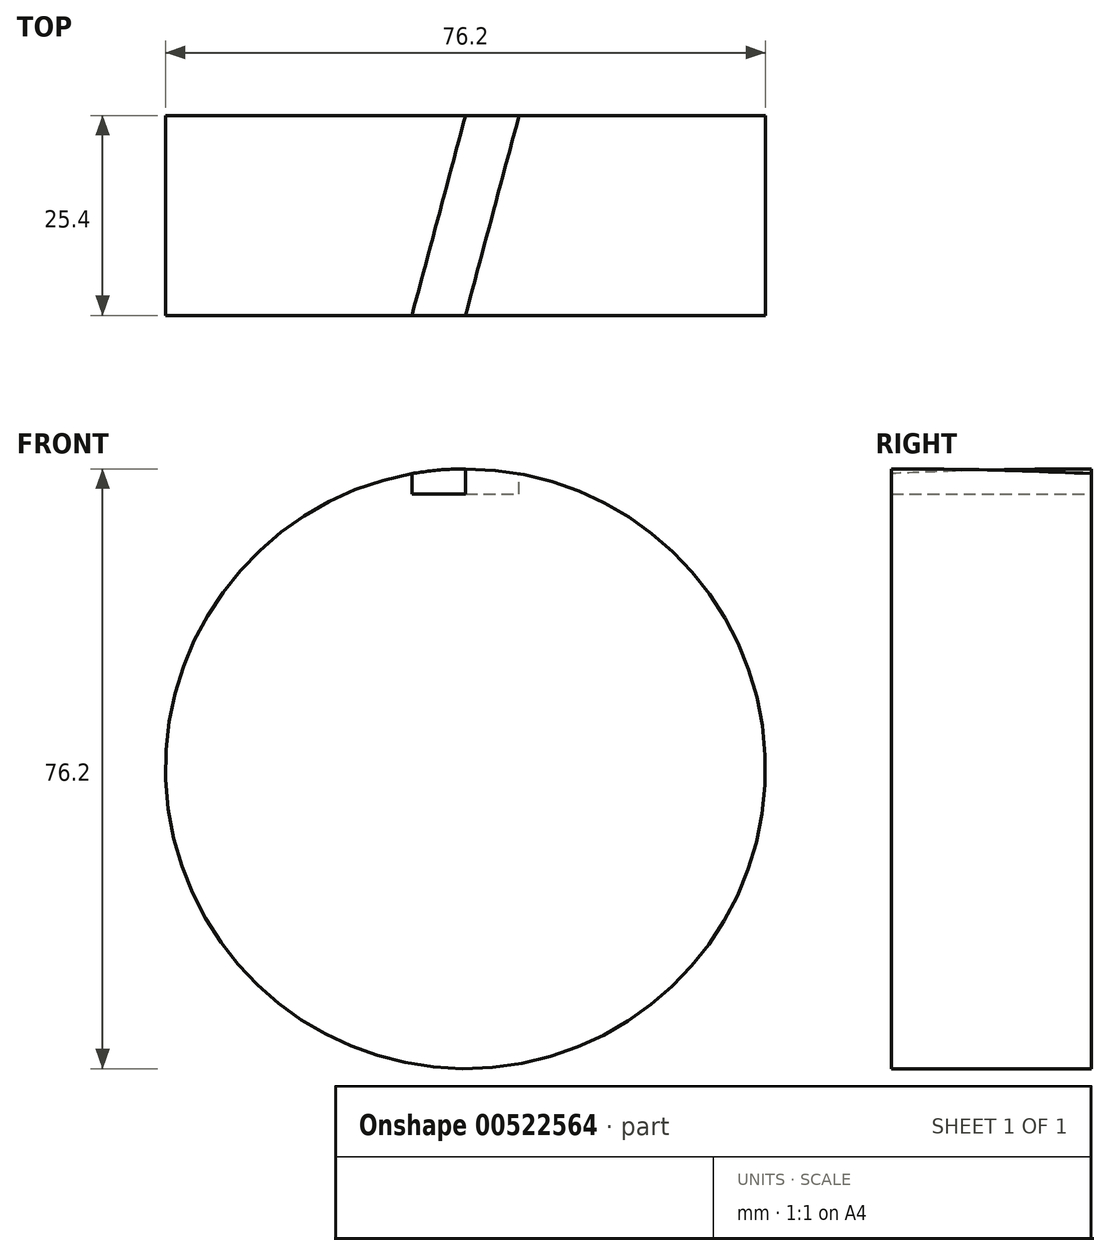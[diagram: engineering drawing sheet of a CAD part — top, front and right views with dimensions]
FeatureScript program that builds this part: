
annotation { "Feature Type Name" : "Feature", "Feature Type Description" : "" }
export const myFeature = defineFeature(function(context is Context, id is Id, definition is map)
    precondition{}
    {
        {
            var Q0;
            Q0=qCreatedBy(makeId("Front.planeOp"),FACE);
            var sketch = newSketch(context, id + "F0", { "sketchPlane" : qUnion([Q0])});
            skCircle(sketch, "E0", {"center": v(0, 0) * mm, "radius": 38.1 * mm});
            skSolve(sketch);
        }
        {
            var Q0;
            Q0 = qSketchRegion(id + "F0", true);
            extrude(context, id + "F1", {"entities" : qUnion([Q0]), "endBound" : BoundingType.SYMMETRIC, "depth" : 25.4 * mm, "offsetDistance" : 25.4 * mm});
        }
        {
            var Q0;
            Q0=qCreatedBy(makeId("Top.planeOp"),FACE);
            cPlane(context, id + "F2", {"entities" : qUnion([Q0]), "cplaneType" : CPlaneType.OFFSET, "offset" : 38.1 * mm, "width" : 152.4 * mm, "height" : 152.4 * mm});
        }
        {
            var Q0;
            Q0=qCreatedBy(id+"F2.planeOp",FACE);
            var sketch = newSketch(context, id + "F3", { "sketchPlane" : qUnion([Q0])});
            skLineSegment(sketch, "E1", {"start": v(0, -12.7) * mm, "end": v(-6.8, -12.7) * mm});
            skLineSegment(sketch, "E2", {"start": v(-6.8, -12.7) * mm, "end": v(0, 12.7) * mm});
            skLineSegment(sketch, "E3", {"start": v(6.8, 12.7) * mm, "end": v(0, -12.7) * mm});
            skLineSegment(sketch, "E4", {"start": v(0, 12.7) * mm, "end": v(6.8, 12.7) * mm});
            skSolve(sketch);
        }
        {
            var Q0;
            Q0 = qSketchRegion(id + "F3", true);
            extrude(context, id + "F4", {"entities" : qUnion([Q0]), "operationType" : NewBodyOperationType.REMOVE, "oppositeDirection" : true, "depth" : 3.17 * mm, "offsetDistance" : 25.4 * mm});
        }
    });
